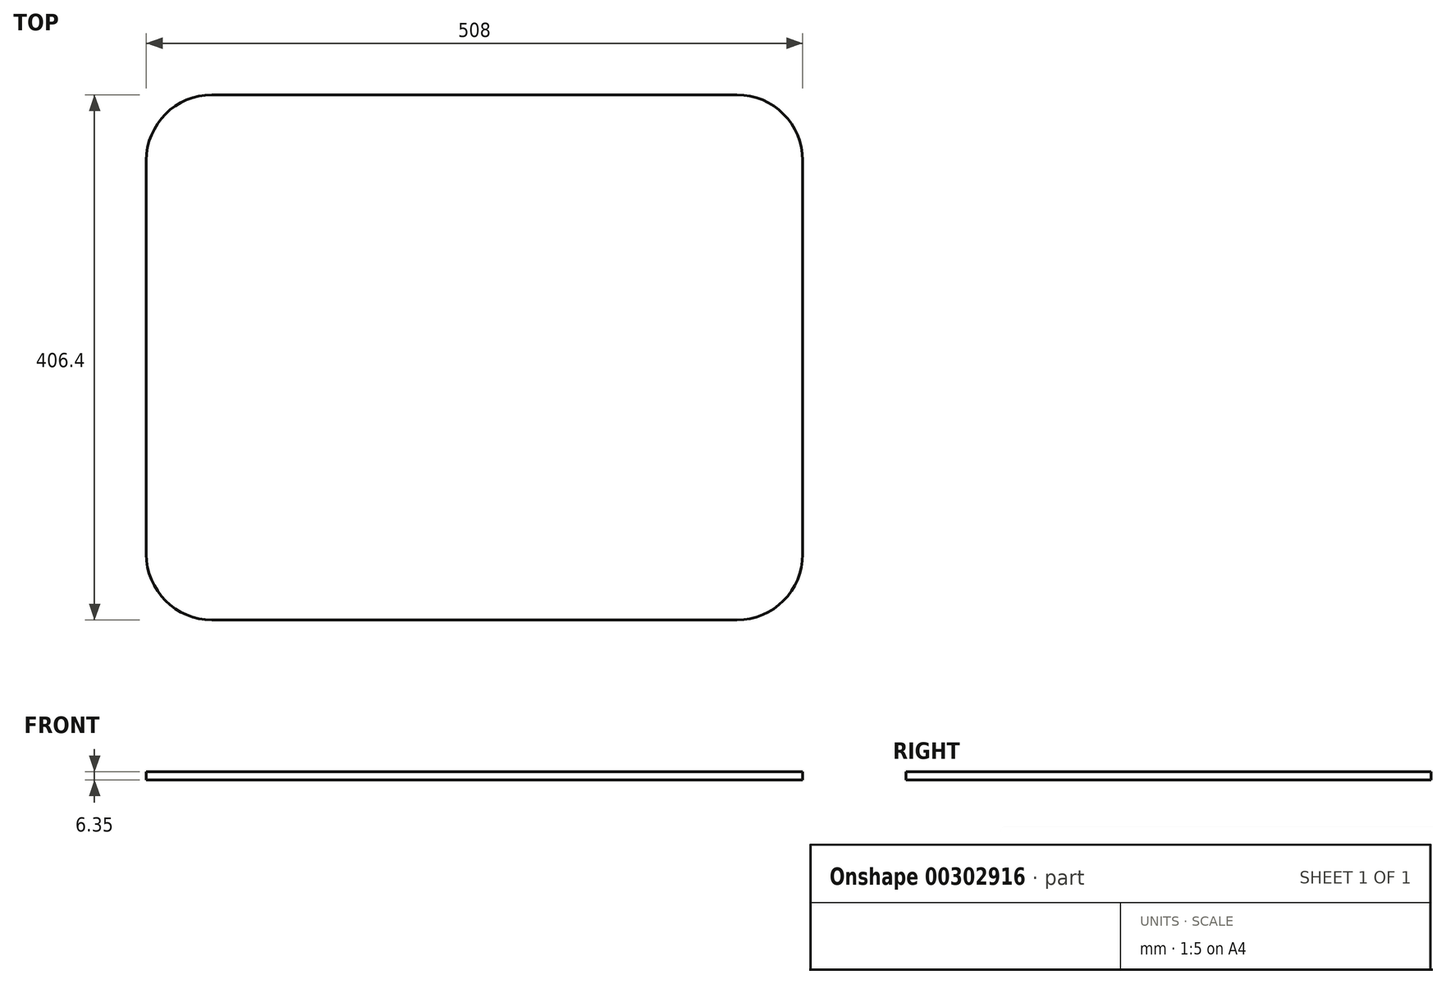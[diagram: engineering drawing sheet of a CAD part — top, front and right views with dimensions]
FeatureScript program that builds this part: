
annotation { "Feature Type Name" : "Feature", "Feature Type Description" : "" }
export const myFeature = defineFeature(function(context is Context, id is Id, definition is map)
    precondition{}
    {
        {
            var Q0;
            Q0=qCreatedBy(makeId("Top.planeOp"),FACE);
            var sketch = newSketch(context, id + "F0", { "sketchPlane" : qUnion([Q0])});
            skLineSegment(sketch, "E0.bottom", {"start": v(203.2, 203.2) * mm, "end": v(-203.2, 203.2) * mm});
            skLineSegment(sketch, "E0.top", {"start": v(203.2, -203.2) * mm, "end": v(-203.2, -203.2) * mm});
            skLineSegment(sketch, "E0.left", {"start": v(254, 152.4) * mm, "end": v(254, -152.4) * mm});
            skLineSegment(sketch, "E0.right", {"start": v(-254, 152.4) * mm, "end": v(-254, -152.4) * mm});
            skPoint(sketch, "E0.middle", {"position": v(0, 0) * mm});
            skPoint(sketch, "E1.visualSharp", {"position": v(-254, -203.2) * mm});
            skArc(sketch, "E1.filletArc", {"start": v(-254, -152.4) * mm, "mid": v(-239.12, -188.32) * mm, "end": v(-203.2, -203.2) * mm});
            skPoint(sketch, "E2.visualSharp", {"position": v(-254, 203.2) * mm});
            skArc(sketch, "E2.filletArc", {"start": v(-203.2, 203.2) * mm, "mid": v(-239.12, 188.32) * mm, "end": v(-254, 152.4) * mm});
            skPoint(sketch, "E3.visualSharp", {"position": v(254, 203.2) * mm});
            skArc(sketch, "E3.filletArc", {"start": v(254, 152.4) * mm, "mid": v(239.12, 188.32) * mm, "end": v(203.2, 203.2) * mm});
            skPoint(sketch, "E4.visualSharp", {"position": v(254, -203.2) * mm});
            skArc(sketch, "E4.filletArc", {"start": v(203.2, -203.2) * mm, "mid": v(239.12, -188.32) * mm, "end": v(254, -152.4) * mm});
            skSolve(sketch);
        }
        {
            var Q0;
            Q0=makeQuery(id+"F0.imprint","IMPRINT",FACE,{"disambiguationData":[TD([[makeQuery(id+"F0.imprint","IMPRINT",EDGE,{"derivedFrom":sQuery(id+"F0.wireOp",EDGE,"E0.bottom")}),1.0]])]});
            extrude(context, id + "F1", {"entities" : qUnion([Q0]), "depth" : 6.35 * mm});
        }
    });
